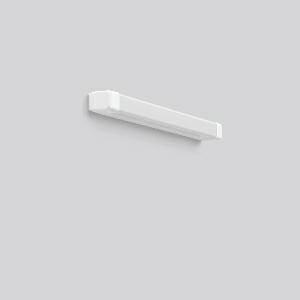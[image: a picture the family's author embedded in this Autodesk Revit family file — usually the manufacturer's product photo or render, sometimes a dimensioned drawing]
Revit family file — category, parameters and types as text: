
# Revit family: baleva_451201_002_2_4d42
name_source: partatom
category: Lighting Fixtures
units: mm (PartAtom-declared; Revit-internal decimal feet)

## family parameters
Cut with Voids When Loaded = No
Host = Face
Light Source = No
Part Type = Normal
Room Calculation Point = No
Round Connector Dimension = Use Diameter
Shared = No

## types (1)
- MultiColor 830 (1 x LED Modul 830, 1050 lm, 3000)
    Apparent Load = 10 VA
    CIE Flux Codes = 40 69 88 82 100
    Color Rendering = 80
    Color Temperature = 3000
    Default Elevation = 1800 mm
    Description = Series: BALEVA
Linear luminaire with timeless functional design. Ideal for sanitary areas, corridors, waiting areas, nursing homes, patient rooms. Body and end caps made of white plastic. Diffuser made of plastic (polycarbonate), opal, shockproof. Homogeneous and smooth light distribution. MultiColour: With rear switching element, variable colour temperature 3000  K or 4000  K. Factory setting is 4000 K. Diffuser can be assembled without the use of tools. Quick and easy to install. Can be installed horizontally and vertically. 2 central cable inlets for looping the cable. Converter integrated and encapsulated. 
Colour: white
Length: 600 mm
Width: 46 mm
Height: 60 mm
Lamp: LED
Socket: without socket
Colour temperature: 3000K, 4000K
Colour rendering index (CRI): 80
System power: 10 W
Rated luminous flux: 1050 lm
Luminous efficiency: 105 lm/W
System power 2: 10 W
Rated luminous flux 2: 1100 lm
Luminous efficiency 2: 110 lm/W
Control gear: Regulated power supply
Protection class: II
Type of protection: IP 40
    Height = 60 mm  [stored 0.19685 ft]
    Lamp = 1 x LED Modul 830
    Lamp Light Flux = 1050 lm
    Lamp count = 1
    Length = 600 mm
    Lifetime = 50000 h
    Luminous efficacy = 105 lm/W
    Manufacturer = RZB
    ModVariant = No
    Model = 451201.002.2
    Mounting Place = Wall, Ceiling
    Mounting Type = Surface mounted
    Number of Poles = 1
    OnlyDefault = Yes
    Power Factor = 1
    Product Name = BALEVA
    Product group = Surface mounted ceiling and wall luminaires
    ProductGroupID = 305
    Protection Class = Protection class II
    Protection Degree = IP 40
    RLX_Detail_Level = 1
    RLX_Emergency_Light_Flux = 0 lm
    RLX_Emergency_Type = 0
    RLX_Emergency_Type_DB = No
    RlxData = <blob elided: 38601 chars, md5=e3e1a0f7>
    Socket = socket
    Standby Power = 0 W
    System Light Flux = 1050 lm
    System Power = 10 W
    Type Comments = MultiColor 830
    Type Image = 451201.002.jpg
    URL = http://relux.com
    VarID = multicolor_830
    Voltage = 230 V
    Voltage Range = 220-240 V
    Weight = 0.00 kg
    Width = 46 mm

note: [stored X ft] marks values corroborated as IEEE doubles in the binary element streams (Revit-internal decimal feet)

## geometry (parser evidence)
native form markers: Blend x4, Sweep x11
no freeform markers — native parametric forms only
